# Revit family: PG_EINBAU_V2
name_source: partatom
category: Allgemeines Modell
revit_build: Autodesk Revit 2018 (Build: 20170223_1515(x64)
units: mm (PartAtom-declared; Revit-internal decimal feet)

## family parameters
Beim Laden mit Abzugskörper schneiden = Ja
Bemaßung runder Anschluss = Durchmesser verwenden
Gemeinsam genutzt = Ja
Kann Basisbauteil für Bewehrung sein = Nein
Raumberechnungspunkt = Nein
Teiletyp = Normal

## types (1)
- MEARIN PG EVO-V1_2 Mörtelbett
    Artikelnummer = 010141803
    Ausführungsunterlagen = gemäß Zeichnung und Einzelbeschreibung
    Bauelement = Entwässerungsrinnen Oberflächenwasser
    Baustoff,Bettung/Fundament = PCC-Mörtel/Epoxy-Mörtel
    Bauteil, Entwässerung = Entwässerungsrinne
    Belastungsklasse Entwässerungsbauteil = C 250
    Beschreibung = Monolithische Entwässerungsrinnen aus Glasfaser-Verbundstoff, Baubreite 180 / 170 mm. Geringe Bauhöhe 30 mm und Reduzierung der Stoßabdichtung durch Länge 3000 mm. Ausführungen mit Andicht-Flansch für OS-Einbau oder ohne Andicht-Flansch für Gussasphalt-Einbau. Standardmäßig erhältlich in 3 Farben (Grau, Schwarz, Rot), weitere Farben auf Anfrage, ab 1000 m Rinne. Brandverhalten gemäß DIN EN 13501-1 Bfl-S1, schwer entflammbar, Nr. 230011568-3.
    Breite = 180 mm  [stored 0.590551 ft]
    Einbautechnologie = Rinne allein
    Gewicht = siehe Dichte Mörtel
    Hersteller = MEA Bautechnik GmbH Geschäftsbereich MEA Water Management
    IfcDescription = Monolithische Entwässerungsrinnen aus Glasfaser-Verbundstoff, Baubreite 180 / 170 mm. Geringe Bauhöhe 30 mm und Reduzierung der Stoßabdichtung durch Länge 3000 mm. Ausführungen mit Andicht-Flansch für OS-Einbau oder ohne Andicht-Flansch für Gussasphalt-Einbau. Standardmäßig erhältlich in 3 Farben (Grau, Schwarz, Rot), weitere Farben auf Anfrage, ab 1000 m Rinne. Brandverhalten gemäß DIN EN 13501-1 Bfl-S1, schwer entflammbar, Nr. 230011568-3.
    IfcExportAs = IfcWasteTerminalType
    IfcExportType = USERDEFINED
    Konstruktion Entwässerungsbauteil = Kammrinne
    MEA Planungshilfe = https://www.mea-group.com
    Nennweite = 150 mm  [stored 0.492126 ft]
    Nennweite mm Entwässerungsbauteil = 150
    STLB-Bau Mustervorlage = https://www.stlb-bau-online.de
    Technische Produktinformation = https://www.mea-group.com
    Typ Entwässerungsbauteil = Typ M
    URL = https://www.mea-group.com
    guid = cf6c1bd8-9bf4-4563-8c57-07955e2378ac

note: [stored X ft] marks values corroborated as IEEE doubles in the binary element streams (Revit-internal decimal feet)
